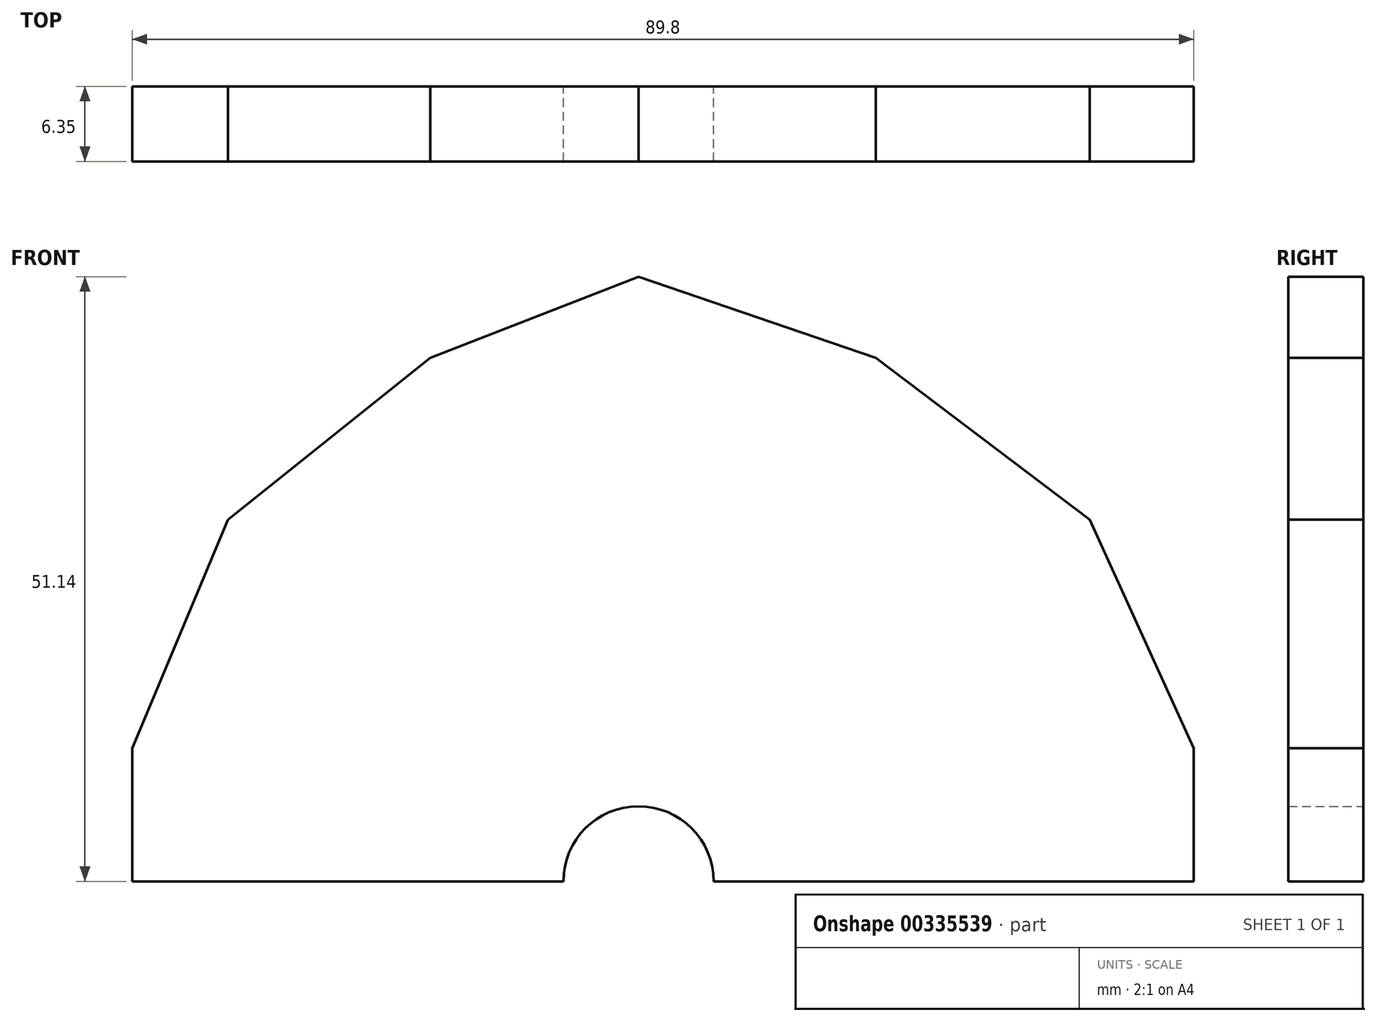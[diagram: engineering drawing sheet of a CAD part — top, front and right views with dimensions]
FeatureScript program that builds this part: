
annotation { "Feature Type Name" : "Feature", "Feature Type Description" : "" }
export const myFeature = defineFeature(function(context is Context, id is Id, definition is map)
    precondition{}
    {
        {
            var Q0;
            Q0=qCreatedBy(makeId("Front.planeOp"),FACE);
            var sketch = newSketch(context, id + "F0", { "sketchPlane" : qUnion([Q0])});
            skLineSegment(sketch, "E0", {"start": v(0, 51.14) * mm, "end": v(0, 0) * mm});
            skLineSegment(sketch, "E1", {"start": v(0, 0) * mm, "end": v(20.06, 44.29) * mm});
            skLineSegment(sketch, "E2", {"start": v(20.06, 44.29) * mm, "end": v(38.17, 30.58) * mm});
            skLineSegment(sketch, "E3", {"start": v(38.17, 30.58) * mm, "end": v(0, 0) * mm});
            skLineSegment(sketch, "E4", {"start": v(0, 0) * mm, "end": v(46.98, 11.26) * mm});
            skLineSegment(sketch, "E5", {"start": v(46.98, 11.26) * mm, "end": v(46.98, 0) * mm});
            skLineSegment(sketch, "E6", {"start": v(46.98, 0) * mm, "end": v(0, 0) * mm});
            skLineSegment(sketch, "E7", {"start": v(-17.62, 44.29) * mm, "end": v(0, 0) * mm});
            skLineSegment(sketch, "E8", {"start": v(-17.62, 44.29) * mm, "end": v(-34.72, 30.58) * mm});
            skLineSegment(sketch, "E9", {"start": v(-34.72, 30.58) * mm, "end": v(0, 0) * mm});
            skLineSegment(sketch, "E10", {"start": v(0, 0) * mm, "end": v(-42.82, 11.26) * mm});
            skLineSegment(sketch, "E11", {"start": v(-42.82, 11.26) * mm, "end": v(-42.82, 0) * mm});
            skLineSegment(sketch, "E12", {"start": v(-42.82, 0) * mm, "end": v(0, 0) * mm});
            skLineSegment(sketch, "E13", {"start": v(-17.62, 44.29) * mm, "end": v(0, 51.14) * mm});
            skLineSegment(sketch, "E14", {"start": v(20.06, 44.29) * mm, "end": v(0, 51.14) * mm});
            skLineSegment(sketch, "E15", {"start": v(-34.72, 30.58) * mm, "end": v(-42.82, 11.26) * mm});
            skLineSegment(sketch, "E16", {"start": v(38.17, 30.58) * mm, "end": v(46.98, 11.26) * mm});
            skSolve(sketch);
        }
        {
            var Q0;
            Q0 = qSketchRegion(id + "F0", true);
            extrude(context, id + "F1", {"entities" : qUnion([Q0]), "depth" : 6.35 * mm});
        }
        {
            var Q0;
            Q0=qCreatedBy(makeId("Front.planeOp"),FACE);
            var sketch = newSketch(context, id + "F2", { "sketchPlane" : qUnion([Q0])});
            skCircle(sketch, "E17", {"center": v(0, 0) * mm, "radius": 7.55 * mm});
            skLineSegment(sketch, "E18", {"start": v(0, 0) * mm, "end": v(7.55, 0) * mm});
            skLineSegment(sketch, "E19", {"start": v(7.55, 0) * mm, "end": v(-7.55, 0) * mm});
            skSolve(sketch);
        }
        {
            var Q0;
            Q0=sQuery(id+"F2.wireOp",VERTEX,"E17.center");
            var Q1;
            Q1=makeQuery(id+"F1.opExtrude","SWEPT_BODY",BODY,{"disambiguationData":[OSD([sQuery(id+"F0.wireOp",EDGE,"E2"),sQuery(id+"F0.wireOp",EDGE,"E5"),sQuery(id+"F0.wireOp",EDGE,"E6"),sQuery(id+"F0.wireOp",EDGE,"E8"),sQuery(id+"F0.wireOp",EDGE,"E11"),sQuery(id+"F0.wireOp",EDGE,"E12"),sQuery(id+"F0.wireOp",EDGE,"E13"),sQuery(id+"F0.wireOp",EDGE,"E14"),sQuery(id+"F0.wireOp",EDGE,"E15"),sQuery(id+"F0.wireOp",EDGE,"E16")])]});
            hole(context, id + "F3", {"style" : HoleStyle.SIMPLE, "endStyle" : HoleEndStyle.THROUGH, "oppositeDirection" : true, "holeDiameter" : 12.7 * mm, "tappedDepth" : 12.7 * mm, "tapClearance" : 3, "locations" : qUnion([Q0]), "scope" : qUnion([Q1])});
        }
    });
